# Revit family: LBA12
name_source: partatom
category: Equipement spécialisé
revit_build: Autodesk Revit 2017 (Build: 20160225_1515(x64)
units: mm (PartAtom-declared; Revit-internal decimal feet)

## family parameters
Basée sur le plan de construction = Non
Cote de connecteur circulaire = Utiliser le diamètre
Couper avec des vides une fois chargée = Non
Partagée = Non
Point de calcul de pièce = Non
Toujours verticalement = Oui
Type d'élément = Normal

## types (3) — shared parameters
Fabricant = La Barrière Automatique
H_FX = 200 mm  [stored 0.656168 ft]
Origine_GA = 175 mm  [stored 0.574147 ft]
URL = https://barriere-automatique.com
Visibilité_Support = Oui
W = 155 mm  [stored 0.50853 ft]
diamètre_bareau_GA = 25 mm  [stored 0.082021 ft]
diamètre_grillage_GA = 15 mm  [stored 0.0492126 ft]
distance_entre_barreau = 200 mm  [stored 0.656168 ft]
distance_entre_grilles_GA = 390 mm
décalage sous lisse_GA = 130 mm  [stored 0.426509 ft]
epaisseur_lisse = 118 mm  [stored 0.387139 ft]
epaisseur_repose_barrière_V = 75 mm  [stored 0.246063 ft]
h_GA = 783 mm  [stored 2.5689 ft]
h_axe_chapeau = 150 mm
h_chapeau = 1023 mm  [stored 3.3563 ft]
h_repose_barrière = 933 mm  [stored 3.06102 ft]
hauteur_grille_HP = 900 mm  [stored 2.95276 ft]
hauteur_lisse = 180 mm  [stored 0.590551 ft]
largeur_borne = 490 mm  [stored 1.60761 ft]
largeur_chapeau = 490 mm  [stored 1.60761 ft]
longueur_borne = 420 mm  [stored 1.37795 ft]
longueur_chapeau = 420 mm  [stored 1.37795 ft]
matériau_bandes_rouges = Plastique, rouge reflet
matériau_base = BLANC_MAT
matériau_borne = Stratifié, bleu marine
matériau_chapeau = BLANC_MAT
matériau_lisse = BLANC_MAT
matériau_repose_barrière = POSTE SUPPORT
origine_grille_HP = 50 mm  [stored 0.164042 ft]
position_grille1_GA = 195 mm

## per-type parameters (varying)
| type | Modèle | Nombre_barreaux_GA | Visibilité_GA | Visibilité_GTH | Visibilité_HP | entreaxe_massifs | h_GTH | longueur_GA | longueur_HP | longueur_lisse | origine_GTH |
| LBA12_lisse_HP 6000 | LBA 12 HP | 11 | Oui | Non | Oui | 6340 mm  [stored 20.8005 ft] | 1000 mm  [stored 3.28084 ft] | 5825 mm | 5925 mm  [stored 19.439 ft] | 6000 mm  [stored 19.685 ft] | 210 mm  [stored 0.688976 ft] |
| LBA12_lisse_GTH 7000 | LBA 12 GTH | 11 | Non | Oui | Non | 7291 mm  [stored 23.9206 ft] | 1740 mm  [stored 5.70866 ft] | 6825 mm | 6925 mm  [stored 22.7198 ft] | 7000 mm  [stored 22.9659 ft] | 350 mm  [stored 1.14829 ft] |
| LBA12_lisse_GA 9000 | LBA 12 GA | 15 | Oui | Non | Non | 9291 mm  [stored 30.4823 ft] | 1000 mm  [stored 3.28084 ft] | 8825 mm | 8925 mm  [stored 29.2815 ft] | 9000 mm | 210 mm  [stored 0.688976 ft] |

note: [stored X ft] marks values corroborated as IEEE doubles in the binary element streams (Revit-internal decimal feet)
